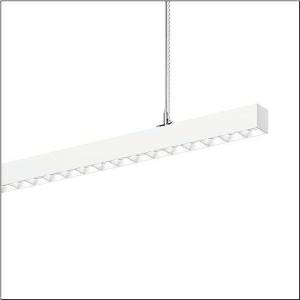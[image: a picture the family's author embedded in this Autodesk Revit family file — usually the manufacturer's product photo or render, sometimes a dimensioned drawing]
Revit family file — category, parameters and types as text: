
# Revit family: silica_21_51mx37da47wb
name_source: partatom
category: Lighting Fixtures
units: mm (PartAtom-declared; Revit-internal decimal feet)

## family parameters
Cut with Voids When Loaded = No
Host = Face
Light Source = No
Part Type = Normal
Room Calculation Point = No
Round Connector Dimension = Use Diameter
Shared = No

## types (1)
- --- (1 x LED, 7300 lm, 44 W, 4000K)
    Apparent Load = 44 VA
    CIE Flux Codes = 71 92 99 59 100
    Color Rendering = 80
    Color Temperature = 4000K
    Default Elevation = 1800 mm
    Description = Silica 21, office luminaire, primary light control with darklight reflector, of PMMA, white, CAT 2 (L<= 3000cd/m²), light emission: direct/indirect distribution, primary light characteristic: asymmetric, installation type: suspended mounting, LED, rated luminous flux: 7.300lm, luminous efficacy: 166lm/W, light colour: 840, colour temperature: 4000K, control gear: DALI 2, with terminal, 3+2-pole, max. 2.5mm², mains connection: 220..240V, AC, 50/60Hz, rated input power: 44W, luminaire housing, of aluminium, traffic white (RAL 9016), length: 1.204mm, width: 53mm, height: 53mm, protection rating (complete): IP20, insulation class (complete): insulation class I (protective earthing), certification: CE, permissible operating ambient temperature: 0..+35°C, standard: EN 50419, packaging unit: 1 piece
    Height = 53 mm
    Lamp = 1 x LED
    Lamp Light Flux = 7300 lm
    Lamp Power = 44 W
    Lamp count = 1
    Length = 1204 mm
    Luminous efficacy = 166 lm/W
    Manufacturer = Siteco
    ModVariant = No
    Model = 51MX37DA47WB
    Mounting Place = Ceiling
    Mounting Type = Pendant
    Number of Poles = 1
    OnlyDefault = Yes
    Power Factor = 1
    Product Name = Silica 21
    Product group = office luminaire | ceiling pendant
    ProductGroupID = 903
    Protection Class = Protection class I
    Protection Degree = IP 20
    RLX_Detail_Level = 1
    RLX_Emergency_Light_Flux = 0 lm
    RLX_Emergency_Type = 0
    RLX_Emergency_Type_DB = No
    RlxData = <blob elided: 42025 chars, md5=42097f90>
    Socket = socket
    Standby Power = 0 W
    System Light Flux = 7300 lm
    System Power = 44 W
    Type Comments = factory setting: luminous flux: 100 % | dim-lin: 254 | 368 mA
    Type Image = l_1335921.jpg
    URL = http://relux.com
    VarID = @adj_119841
    Voltage = 0 V
    Weight = 0.00 kg
    Width = 53 mm

## geometry (parser evidence)
native form markers: Blend x4, Sweep x10
no freeform markers — native parametric forms only
